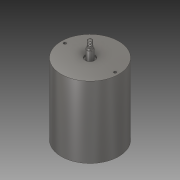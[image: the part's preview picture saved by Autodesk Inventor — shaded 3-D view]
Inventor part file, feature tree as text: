
AUTODESK INVENTOR PART (.ipt)
format: ipt  version: 2019 (Build 230136000, 136)  size: 671,744 bytes
history: native  units: mm
features: sketch x10, extrude x5, hole x2, revolve x2, thread x1, helix x1
ambient origin geometry x8: Origin, YZ Plane, XZ Plane, XY Plane, X Axis, Y Axis, Z Axis, Center Point
bodies: Solid1 (feature_tree), Solid2 (feature_tree)
feature tree (21):
  extrude  "Extrusion1"  Depth=134.0mm TaperAngle=0.0deg
  extrude  "Extrusion2"  Depth=2.5mm TaperAngle=0.0deg
  extrude  "Extrusion3"  Depth=17.0mm TaperAngle=0.0deg
  extrude  "Extrusion4"  Depth=10.0mm
  hole  "Hole1"  [1 undecoded]
  hole  "Hole2"  [1 undecoded]
  extrude  "Extrusion5"  Depth=10.0mm
  thread  "Thread1"  [1 undecoded]
  revolve  "Revolution1"  [1 undecoded]
  revolve  "Revolution2"  [1 undecoded]
  helix  "Coil1"  [1 undecoded]
  sketch  "Sketch1"  dims[d0=108.0mm d1=134.0mm d2=0.0mm]
  sketch  "Sketch2"  dims[d3=18.0mm d4=2.5mm d5=0.0mm]
  sketch  "Sketch3"  dims[d6=12.0mm d7=17.0mm d8=0.0mm]
  sketch  "Sketch4"  dims[d9=10.0mm d10=8.5mm]
  sketch  "Sketch5"  dims[d11=3.5mm d12=0.0mm d16=94.5mm]
  sketch  "Sketch6"  dims[d17=4.917mm d18=10.0mm d19=4.0mm d20=2.0mm d21=90.0deg d22=10.0mm d23=20.594885mm d24=94.5mm]
  sketch  "Sketch7"  dims[d25=4.917mm d26=10.0mm d27=4.0mm d28=2.0mm d29=90.0deg d30=10.0mm d31=20.594885mm d32=8.0mm d33=10.5mm d34=0.0mm]
  sketch  "Sketch8"  dims[d35=10.0mm d36=0.0mm d37=9.599311mm d38=0.200104mm d39=0.200104mm]
  sketch  "Sketch9"  dims[d42=1.25mm d44=9.599311mm d46=0.0mm]
  sketch  "Sketch10"  dims[d47=0.0mm d48=1.25125mm d49=13.0mm d50=10.0mm d51=0.0mm d52=0.0mm d53=0.0mm d54=0.0mm d55=0.0mm]
note: 6 required parameter values undecoded (feature->parameter linkage not recoverable at this tier; creation-order binding heuristic only, values carry confidence <= 0.55)